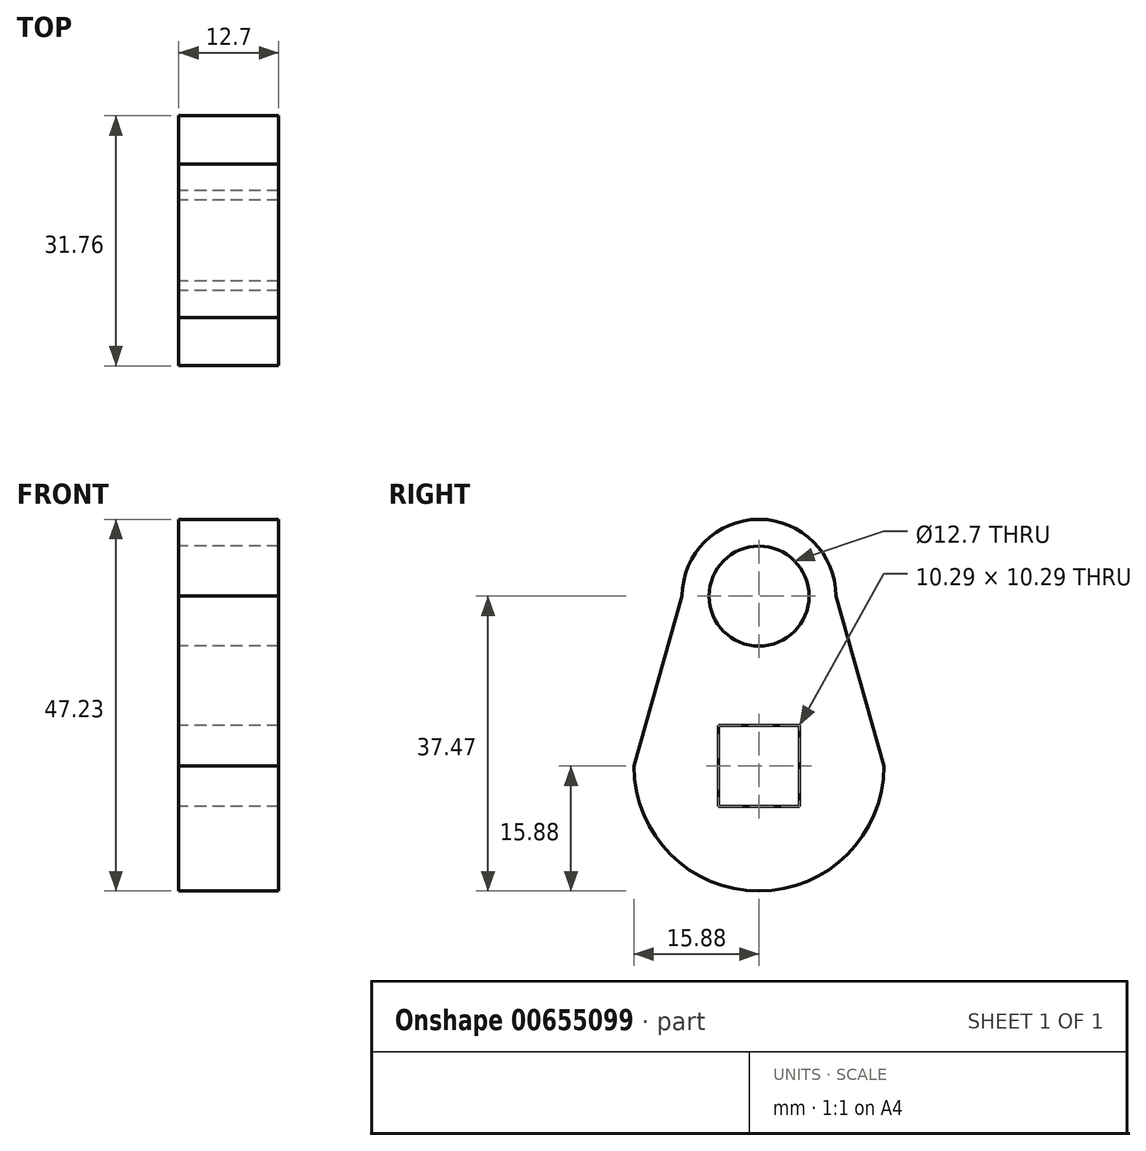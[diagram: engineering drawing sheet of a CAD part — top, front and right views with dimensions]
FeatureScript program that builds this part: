
annotation { "Feature Type Name" : "Feature", "Feature Type Description" : "" }
export const myFeature = defineFeature(function(context is Context, id is Id, definition is map)
    precondition{}
    {
        {
            var Q0;
            Q0=qCreatedBy(makeId("Right.planeOp"),FACE);
            var sketch = newSketch(context, id + "F0", { "sketchPlane" : qUnion([Q0])});
            skLineSegment(sketch, "E0.bottom", {"start": v(-5.14, 5.14) * mm, "end": v(5.14, 5.14) * mm});
            skLineSegment(sketch, "E0.top", {"start": v(-5.14, -5.14) * mm, "end": v(5.14, -5.14) * mm});
            skLineSegment(sketch, "E0.left", {"start": v(-5.14, 5.14) * mm, "end": v(-5.14, -5.14) * mm});
            skLineSegment(sketch, "E0.right", {"start": v(5.14, 5.14) * mm, "end": v(5.14, -5.14) * mm});
            skPoint(sketch, "E0.middle", {"position": v(0, 0) * mm});
            skArc(sketch, "E1", {"start": v(9.76, 21.59) * mm, "mid": v(0, 31.35) * mm, "end": v(-9.76, 21.59) * mm});
            skCircle(sketch, "E2", {"center": v(0, 21.59) * mm, "radius": 6.35 * mm});
            skArc(sketch, "E3.trimOffspring", {"start": v(-15.88, 0) * mm, "mid": v(0, -15.88) * mm, "end": v(15.88, 0) * mm});
            skLineSegment(sketch, "E4", {"start": v(-9.76, 21.59) * mm, "end": v(-15.88, 0) * mm});
            skLineSegment(sketch, "E5", {"start": v(9.76, 21.59) * mm, "end": v(15.87, 0) * mm});
            skSolve(sketch);
        }
        {
            var Q0;
            Q0 = qSketchRegion(id + "F0", true);
            extrude(context, id + "F1", {"entities" : qUnion([Q0]), "depth" : 12.7 * mm, "offsetDistance" : 25.4 * mm});
        }
    });
